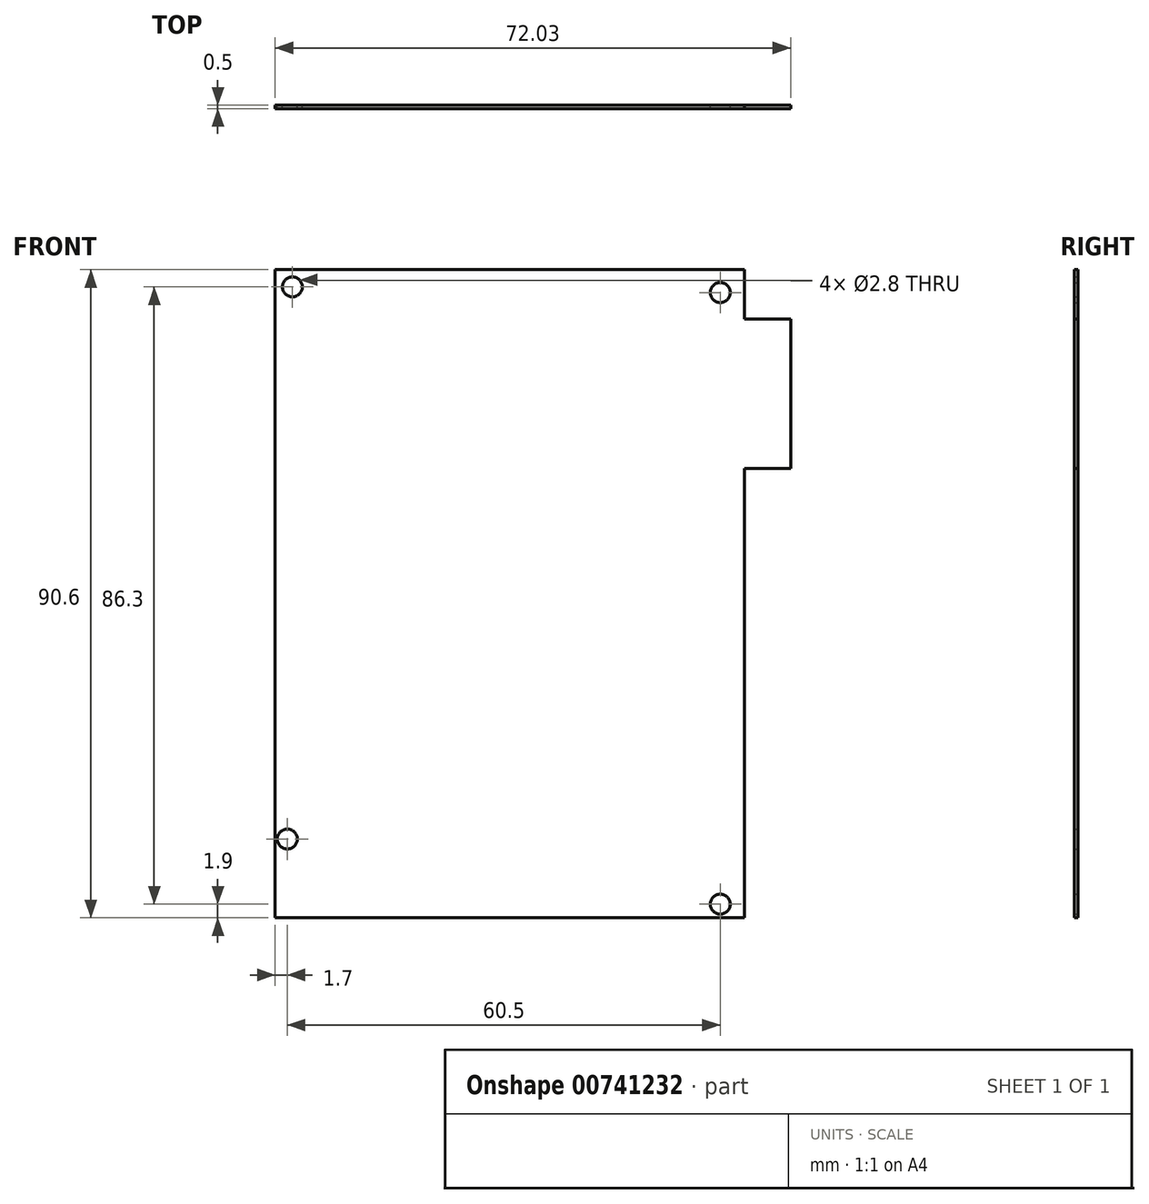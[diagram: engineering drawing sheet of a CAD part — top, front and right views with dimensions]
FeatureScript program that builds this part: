
annotation { "Feature Type Name" : "Feature", "Feature Type Description" : "" }
export const myFeature = defineFeature(function(context is Context, id is Id, definition is map)
    precondition{}
    {
        {
            var Q0;
            Q0=qCreatedBy(makeId("Front.planeOp"),FACE);
            var sketch = newSketch(context, id + "F0", { "sketchPlane" : qUnion([Q0])});
            skLineSegment(sketch, "E0.bottom", {"start": v(32.8, -45.3) * mm, "end": v(-32.8, -45.3) * mm});
            skLineSegment(sketch, "E0.top", {"start": v(32.8, 45.3) * mm, "end": v(-32.8, 45.3) * mm});
            skLineSegment(sketch, "E0.left", {"start": v(32.8, -45.3) * mm, "end": v(32.8, 45.3) * mm});
            skLineSegment(sketch, "E0.right", {"start": v(-32.8, -45.3) * mm, "end": v(-32.8, 45.3) * mm});
            skPoint(sketch, "E0.middle", {"position": v(0, 0) * mm});
            skCircle(sketch, "E1", {"center": v(29.4, 42.1) * mm, "radius": 1.4 * mm});
            skCircle(sketch, "E2", {"center": v(-30.4, 42.9) * mm, "radius": 1.4 * mm});
            skLineSegment(sketch, "E3.bottom", {"start": v(32.8, 38.4) * mm, "end": v(39.23, 38.4) * mm});
            skLineSegment(sketch, "E3.top", {"start": v(32.8, 17.52) * mm, "end": v(39.23, 17.52) * mm});
            skLineSegment(sketch, "E3.left", {"start": v(32.8, 38.4) * mm, "end": v(32.8, 17.52) * mm});
            skLineSegment(sketch, "E3.right", {"start": v(39.23, 38.4) * mm, "end": v(39.23, 17.52) * mm});
            skCircle(sketch, "E4", {"center": v(29.4, -43.4) * mm, "radius": 1.4 * mm});
            skCircle(sketch, "E5", {"center": v(-31.1, -34.3) * mm, "radius": 1.4 * mm});
            skSolve(sketch);
        }
        {
            var Q0;
            {var subQ3=sQuery(id+"F0.wireOp",EDGE,"E0.bottom");Q0=makeQuery(id+"F0.imprint","IMPRINT",FACE,{"disambiguationData":[TD([[makeQuery(id+"F0.imprint","IMPRINT",EDGE,{"derivedFrom":subQ3}),-1.0]])]});}
            var Q1;
            Q1=makeQuery(id+"F0.imprint","IMPRINT",FACE,{"disambiguationData":[TD([[makeQuery(id+"F0.imprint","IMPRINT",EDGE,{"derivedFrom":sQuery(id+"F0.wireOp",EDGE,"E3.bottom")}),-1.0]])]});
            extrude(context, id + "F1", {"entities" : qUnion([Q0, Q1]), "depth" : 0.5 * mm, "offsetDistance" : 25 * mm});
        }
    });
